# Revit family: Shower_Twin_Nero_Project_Round
name_source: partatom
category: Plumbing Fixtures
units: mm (PartAtom-declared; Revit-internal decimal feet)

## family parameters
Always vertical = Yes
Cut with Voids When Loaded = Yes
Maintain Annotation Orientation = No
OmniClass Number = 23.31.17.00
OmniClass Title = Showers
Part Type = Normal
Room Calculation Point = No
Round Connector Dimension = Use Diameter
Shared = No
Work Plane-Based = No

## types (7) — shared parameters
Assembly Code = C1030210
CW Connection = Yes
HW Connection = Yes
IfcExportAs = IfcSanitaryTerminal
IfcExportType = SHOWER
Manufacturer = Nero
ManufacturerOverallDepth = 546 mm  [stored 1.79134 ft]
ManufacturerOverallHeight = 1207.5 mm
ManufacturerOverallWidth = 250 mm
ManufacturerURLProductSpecific = https://nerotapware.com.au
ModifiedIssue = 20240517 $
URL = https://nerotapware.com.au
Uniclass2015Title = Shower fittings package
Vent Connection = No
Waste Connection = No
zero-valued in all types: Default Elevation

## per-type parameters (varying)
| type | BodyMaterial | Description | ManufacturerSpecCode | Model | Type Comments | Uniclass2015Code | Uniclass2015Version |
| Gun Metal 4 Star Rating (NR232105fGM) | Metal_GunMetal_Nero | Round Project Twin Shower 4 Star Rating Gun Metal | NR232105fGM | NR232105fGM | Shower - Twin - Round - Gun Metal | Pr_40_20_87_75 | Products v1.28 |
| Brushed Gold 4 Star Rating (NR232105fBG) | Metal_Gold_Nero_Brushed | Round Project Twin Shower 4 Star Rating Brushed Gold | NR232105fBG | NR232105fBG | Shower - Twin - Round - Brushed Gold | Pr_40_20_87_75 | Products v1.28 |
| Brushed Nickel 4 Star Rating (NR232105fBN) | Metal_Nickel_Nero_Brushed | Round Project Twin Shower 4 Star Rating Brushed Nickel | NR232105fBN | NR232105fBN | Shower - Twin - Round - Brushed Nickel | Pr_40_20_87_75 | Products v1.28 |
| Matte Black 4 Star Rating (NR232105fMB) | Metal_MatteBlack_Nero | Round Project Twin Shower 4 Star Rating Matte Black | NR232105fMB | NR232105fMB | Shower - Twin - Round - Matte Black | Pr_40_20_87_75 | Products v1.28 |
| Chrome 4 Star Rating (NR232105fCH) | Metal_Chrome_Nero | Round Project Twin Shower 4 Star Rating Chrome | NR232105fCH | NR232105fCH | Shower - Twin - Round - Chrome | Pr_40_20_87_75 | Products v1.28 |
| Gun Metal (NR232105DGM) | Metal_GunMetal_Nero | Round Project Twin Shower Gun Metal | NR232105DGM | NR232105DGM | Shower - Twin - Round - Gun Metal | Pr_40_20_87_76 | Products v1.29 |
| Brushed Gold (NR232105DBG) | Metal_Gold_Nero_Brushed | Round Project Twin Shower Brushed Gold | NR232105DBG | NR232105DBG | Shower - Twin - Round - Brushed Gold | Pr_40_20_87_75 | Products v1.28 |

note: [stored X ft] marks values corroborated as IEEE doubles in the binary element streams (Revit-internal decimal feet)

## geometry (parser evidence)
native form markers: Sweep x2
no freeform markers — native parametric forms only
